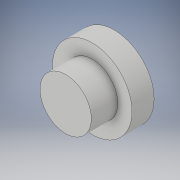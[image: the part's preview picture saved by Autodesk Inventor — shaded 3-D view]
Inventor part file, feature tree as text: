
AUTODESK INVENTOR PART (.ipt)
format: ipt  version: 2019 (Build 230136000, 136)  size: 108,032 bytes
history: native  units: in
note: dims shown in document units (in); Inventor stores cm internally (conversion verified against a paired STEP export)
features: extrude x3, sketch x3
ambient origin geometry x8: Origin, YZ Plane, XZ Plane, XY Plane, X Axis, Y Axis, Z Axis, Center Point
bodies: Solid1 (feature_tree)
feature tree (6):
  extrude  "Extrusion1"  Depth=0.125in TaperAngle=0.0deg
  extrude  "Extrusion2"  Depth=0.05in TaperAngle=0.0deg
  extrude  "Extrusion3"  Depth=0.1in TaperAngle=0.0deg
  sketch  "Sketch1"  dims[d0=0.45in d1=0.125in d2=0.0in]
  sketch  "Sketch2"  dims[d3=0.29in d4=0.05in d5=0.0in]
  sketch  "Sketch3"  dims[d6=0.29in d7=0.1in d8=0.0in]
